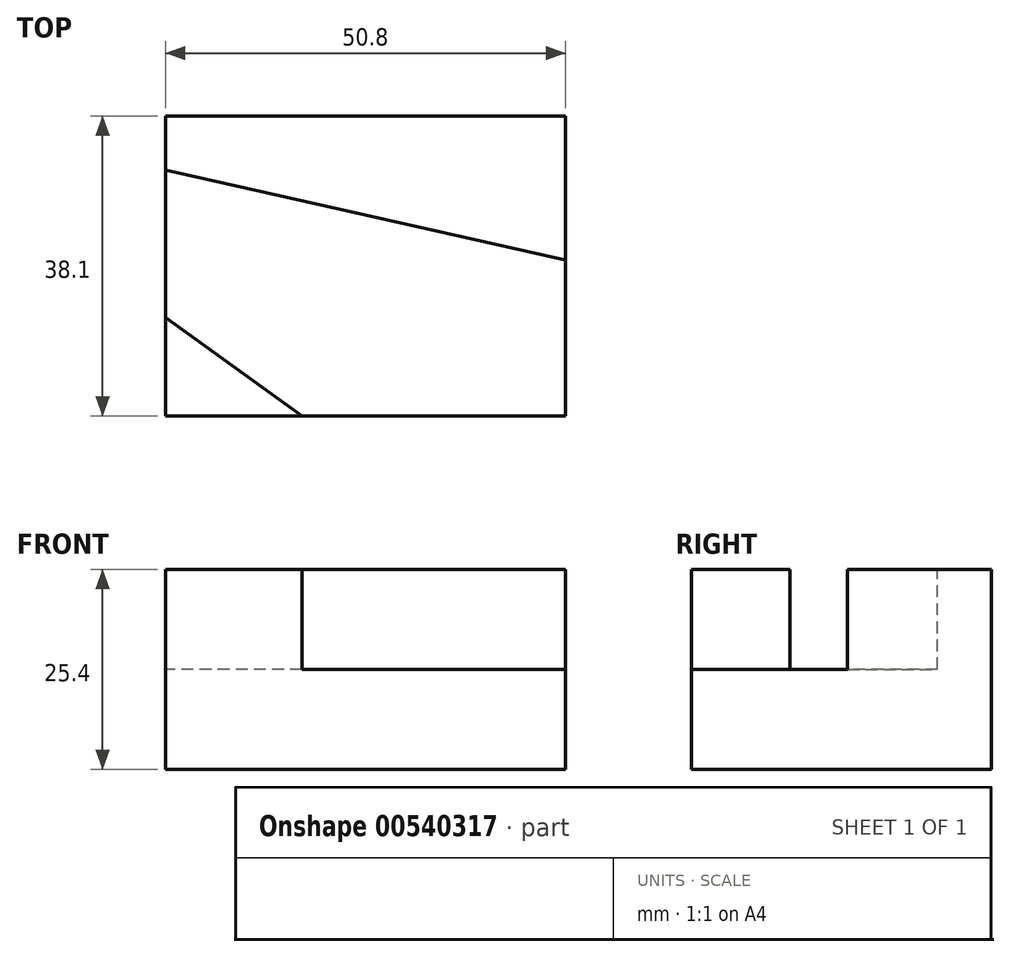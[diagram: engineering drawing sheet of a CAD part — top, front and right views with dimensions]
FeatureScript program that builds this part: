
annotation { "Feature Type Name" : "Feature", "Feature Type Description" : "" }
export const myFeature = defineFeature(function(context is Context, id is Id, definition is map)
    precondition{}
    {
        {
            var Q0;
            Q0=qCreatedBy(makeId("Right.planeOp"),FACE);
            var sketch = newSketch(context, id + "F0", { "sketchPlane" : qUnion([Q0])});
            skLineSegment(sketch, "E0.bottom", {"start": v(0, 0) * mm, "end": v(-38.1, 0) * mm});
            skLineSegment(sketch, "E0.top", {"start": v(0, 25.4) * mm, "end": v(-38.1, 25.4) * mm});
            skLineSegment(sketch, "E0.left", {"start": v(0, 0) * mm, "end": v(0, 25.4) * mm});
            skLineSegment(sketch, "E0.right", {"start": v(-38.1, 0) * mm, "end": v(-38.1, 25.4) * mm});
            skSolve(sketch);
        }
        {
            var Q0;
            Q0 = qSketchRegion(id + "F0", true);
            var Q1;
            Q1=makeQuery(id+"F0.imprint","IMPRINT",FACE,{"disambiguationData":[TD([[makeQuery(id+"F0.imprint","IMPRINT",EDGE,{"derivedFrom":sQuery(id+"F0.wireOp",EDGE,"E0.bottom")}),-1.0]])]});
            extrude(context, id + "F1", {"entities" : qUnion([Q0, Q1]), "depth" : 50.8 * mm, "offsetDistance" : 25.4 * mm});
        }
        {
            var Q0;
            Q0=makeQuery(id+"F1.opExtrude","SWEPT_FACE",FACE,{"disambiguationData":[OSD([sQuery(id+"F0.wireOp",EDGE,"E0.top")])]});
            var sketch = newSketch(context, id + "F2", { "sketchPlane" : qUnion([Q0])});
            skLineSegment(sketch, "E1", {"start": v(0, -25.6) * mm, "end": v(17.32, -38.1) * mm});
            skSolve(sketch);
        }
        {
            var Q0;
            {var subQ3=sQuery(id+"F2.wireOp",EDGE,"E1");Q0=makeQuery(id+"F2.imprint","IMPRINT",FACE,{"disambiguationData":[TD([[makeQuery(id+"F2.imprint","IMPRINT",EDGE,{"derivedFrom":subQ3}),1.0]])]});}
            var sketch = newSketch(context, id + "F3", { "sketchPlane" : qUnion([Q0])});
            skLineSegment(sketch, "E2", {"start": v(50.96, -37.37) * mm, "end": v(50.96, -18.32) * mm});
            skLineSegment(sketch, "E3", {"start": v(50.96, -18.32) * mm, "end": v(0, -6.84) * mm});
            skSolve(sketch);
        }
        {
            var Q0;
            {var subQ3=sQuery(id+"F2.wireOp",EDGE,"E1");var subQ5=makeQuery(id+"F2.imprint","IMPRINT",EDGE,{"derivedFrom":subQ3});Q0=makeQuery(id+"F3.imprint","IMPRINT",FACE,{"disambiguationData":[TD([[makeQuery(id+"F3.imprint","IMPRINT",EDGE,{"derivedFrom":subQ5}),1.0]])]});}
            extrude(context, id + "F4", {"entities" : qUnion([Q0]), "operationType" : NewBodyOperationType.REMOVE, "oppositeDirection" : true, "depth" : 12.7 * mm, "offsetDistance" : 25.4 * mm});
        }
    });
